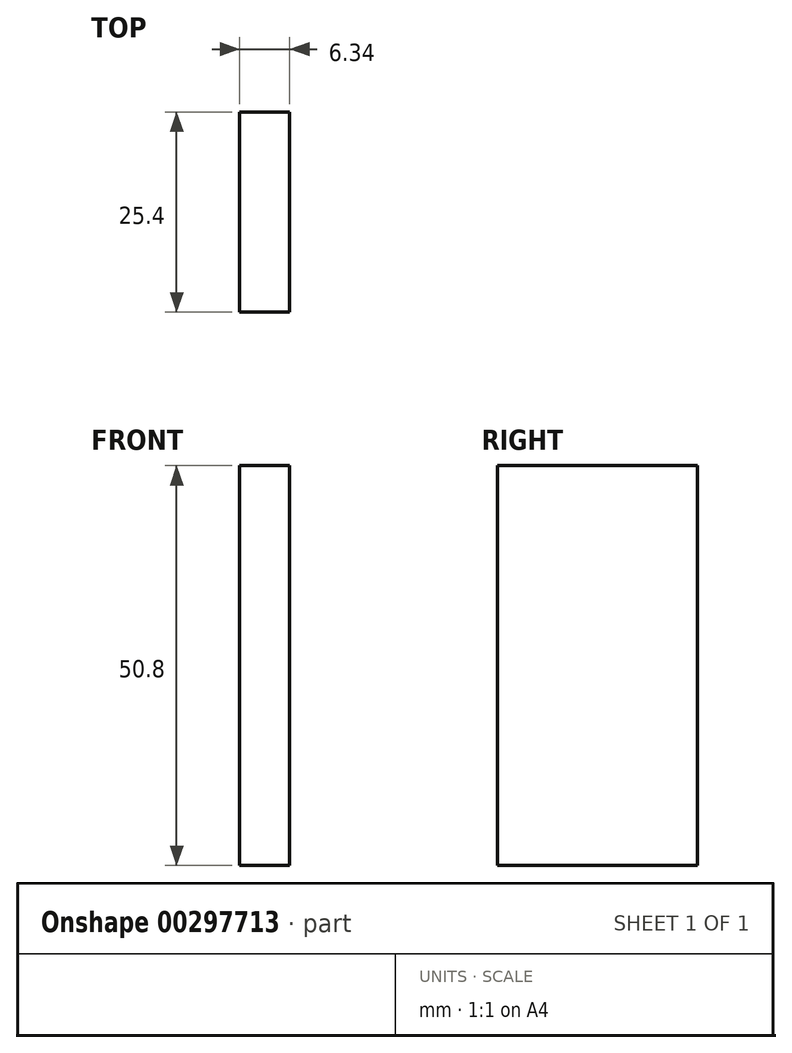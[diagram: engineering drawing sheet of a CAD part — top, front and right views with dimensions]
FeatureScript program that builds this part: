
annotation { "Feature Type Name" : "Feature", "Feature Type Description" : "" }
export const myFeature = defineFeature(function(context is Context, id is Id, definition is map)
    precondition{}
    {
        {
            var Q0;
            Q0=qCreatedBy(makeId("Front.planeOp"),FACE);
            var sketch = newSketch(context, id + "F0", { "sketchPlane" : qUnion([Q0])});
            skLineSegment(sketch, "E0.bottom", {"start": v(3.18, 25.4) * mm, "end": v(-3.17, 25.4) * mm});
            skLineSegment(sketch, "E0.top", {"start": v(3.17, -25.4) * mm, "end": v(-3.18, -25.4) * mm});
            skLineSegment(sketch, "E0.left", {"start": v(3.18, 25.4) * mm, "end": v(3.17, -25.4) * mm});
            skLineSegment(sketch, "E0.right", {"start": v(-3.17, 25.4) * mm, "end": v(-3.18, -25.4) * mm});
            skPoint(sketch, "E0.middle", {"position": v(0, 0) * mm});
            skSolve(sketch);
        }
        {
            var Q0;
            Q0 = qSketchRegion(id + "F0", true);
            extrude(context, id + "F1", {"entities" : qUnion([Q0]), "depth" : 25.4 * mm});
        }
    });
